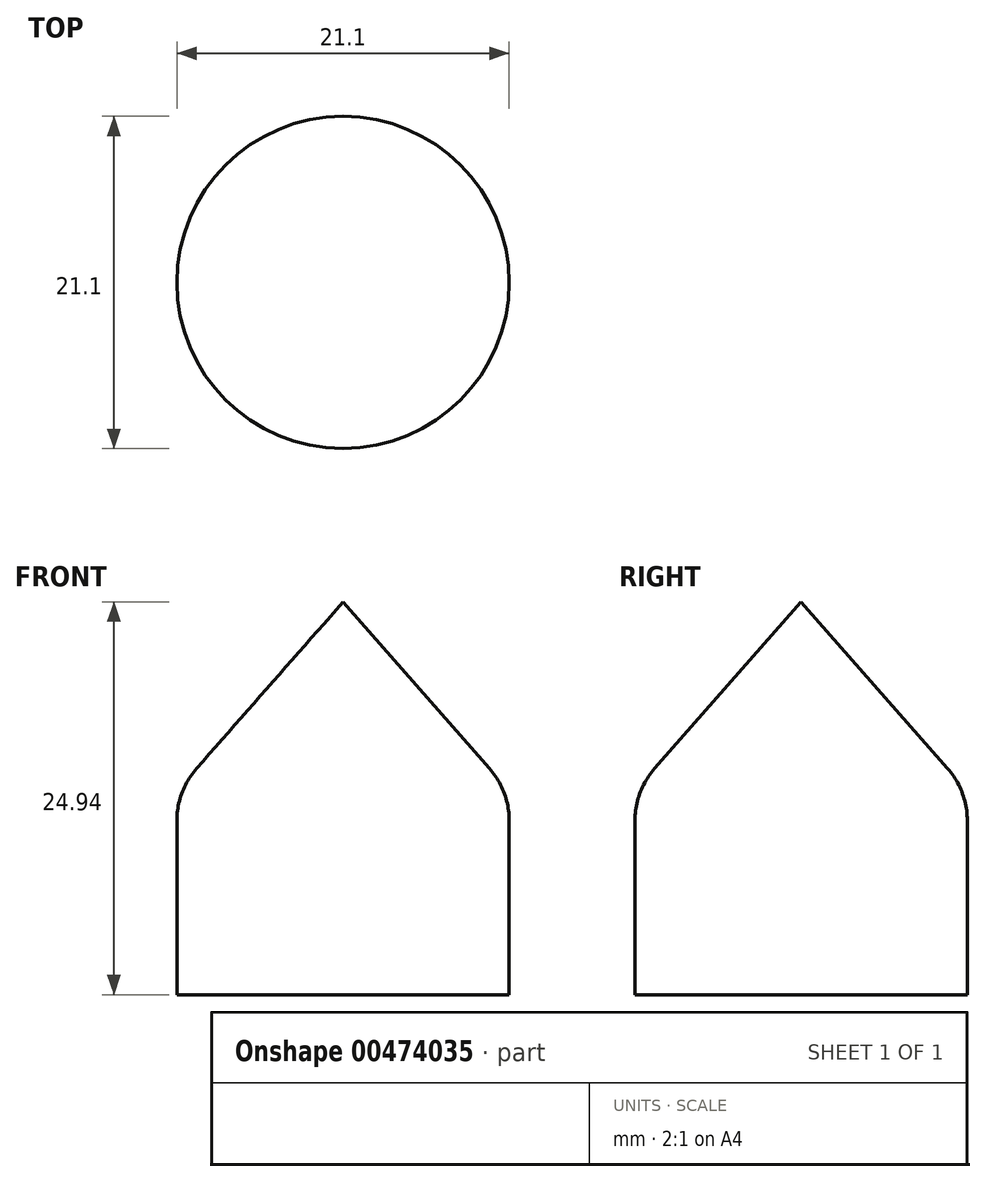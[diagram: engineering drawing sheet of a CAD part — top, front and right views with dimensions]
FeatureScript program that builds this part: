
annotation { "Feature Type Name" : "Feature", "Feature Type Description" : "" }
export const myFeature = defineFeature(function(context is Context, id is Id, definition is map)
    precondition{}
    {
        {
            var Q0;
            Q0=qCreatedBy(makeId("Right.planeOp"),FACE);
            var sketch = newSketch(context, id + "F0", { "sketchPlane" : qUnion([Q0])});
            skLineSegment(sketch, "E0.bottom", {"start": v(-5.08, -12.95) * mm, "end": v(5.47, -12.95) * mm});
            skLineSegment(sketch, "E0.left", {"start": v(-5.08, -12.95) * mm, "end": v(-5.08, 0) * mm});
            skLineSegment(sketch, "E0.right", {"start": v(5.47, -12.95) * mm, "end": v(5.47, 11.99) * mm});
            skPoint(sketch, "E1", {"position": v(-5.08, 0) * mm});
            skLineSegment(sketch, "E2", {"start": v(-5.08, 0) * mm, "end": v(5.47, 11.99) * mm});
            skSolve(sketch);
        }
        {
            var Q0;
            Q0 = qSketchRegion(id + "F0", true);
            var Q1;
            Q1=sQuery(id+"F0.wireOp",EDGE,"E0.right");
            revolve(context, id + "F1", {"entities" : qUnion([Q0]), "axis" : qUnion([Q1]), "revolveType" : RevolveType.FULL});
        }
        {
            var Q0;
            Q0=makeQuery(id+"F1.opRevolve","SWEPT_EDGE",EDGE,{"disambiguationData":[OSD([sQuery(id+"F0.wireOp",EDGE,"E0.left"),sQuery(id+"F0.wireOp",EDGE,"E2")])]});
            fillet(context, id + "F2", {"entities" : qUnion([Q0]), "radius" : 5 * mm, "tangentPropagation" : true, "allowEdgeOverflow" : false});
        }
    });
